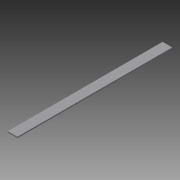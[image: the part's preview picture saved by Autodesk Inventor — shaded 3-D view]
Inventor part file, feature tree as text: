
AUTODESK INVENTOR PART (.ipt)
format: ipt  version: 2015 (Build 190159000, 159)  size: 67,584 bytes
history: native  units: in
note: dims shown in document units (in); Inventor stores cm internally (conversion verified against a paired STEP export)
features: extrude x1, sketch x1
ambient origin geometry x8: Origin, YZ Plane, XZ Plane, XY Plane, X Axis, Y Axis, Z Axis, Center Point
bodies: Solid1 (feature_tree)
feature tree (2):
  extrude  "Extrusion1"  Depth=0.125in
  sketch  "Sketch1"  dims[d0=1.0in d1=0.125in d2=16.0in d3=0.0in]
